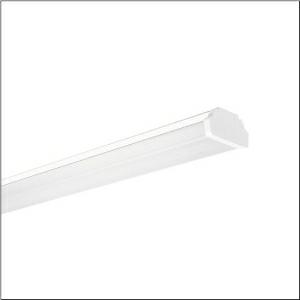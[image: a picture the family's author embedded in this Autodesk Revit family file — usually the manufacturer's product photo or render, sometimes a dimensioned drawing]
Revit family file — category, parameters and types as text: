
# Revit family: dus_r__31_ho_53bd812d2v4120_dd06
name_source: partatom
category: Lighting Fixtures
units: mm (PartAtom-declared; Revit-internal decimal feet)

## family parameters
Cut with Voids When Loaded = No
Host = Face
Light Source = No
Part Type = Normal
Room Calculation Point = No
Round Connector Dimension = Use Diameter
Shared = No

## types (1)
- --- (1 x LED, 12350 lm, 79.5 W, 4000K)
    Apparent Load = 80 VA
    CIE Flux Codes = 47 80 95 92 100
    Color Rendering = 80
    Color Temperature = 4000K
    Default Elevation = 1800 mm
    Description = DUS® 31 HOluminaire insert, length: 1.535mm, width: 81mm, height: 90mm, LED rated luminous flux: 12.350lm, light colour: 840, control gear: DALI 2, control gear: ECG DALI, with plug, 5-pole, with phase selection, mains connection: 220..240V, AC, 50/60Hz, primary optical cover: cover, of PMMA, light emission: direct distribution, primary light characteristic: symmetric, protection rating (complete): IP20, protection rating (LED compartment): IP50, insulation class (complete): insulation class I (protective earthing), certification: CE, ENEC, VDE, permissible ambient temperature for indoor applications: -25..+30°C, corresponds to IFS (International Featured Standards) requirements for safety and quality in the food industry, reducing of maximum allowable ambient temperature of 5°C with ceiling mounting, packaging unit: 1 piece
    Height = 95 mm
    Lamp = 1 x LED
    Lamp Light Flux = 12350 lm
    Lamp Power = 79.5 W
    Lamp count = 1
    Length = 1535 mm
    Luminous efficacy = 155 lm/W
    Manufacturer = Siteco
    ModVariant = No
    Model = 53BD812D2V4120
    Mounting Place = Ceiling
    Mounting Type = Pendant
    Number of Poles = 1
    OnlyDefault = Yes
    Power Factor = 1
    Product Name = DUS® 31 HO
    Product group = luminaire insert
    ProductGroupID = 902
    Protection Class = Protection class I
    Protection Degree = IP 20
    RLX_Detail_Level = 1
    RlxData = <blob elided: 42013 chars, md5=8d0fe4f7>
    Socket = socket
    Standby Power = 0 W
    System Light Flux = 12350 lm
    System Power = 80 W
    Type Comments = factory setting: luminous flux: 100 % | dim-lin: 254 | 345 mA
    Type Image = l_1003451.jpg
    URL = http://relux.com
    VarID = @adj_133545
    Voltage = 0 V
    Weight = 0.00 kg
    Width = 81 mm

## geometry (parser evidence)
native form markers: Blend x4, Sweep x13
no freeform markers — native parametric forms only
